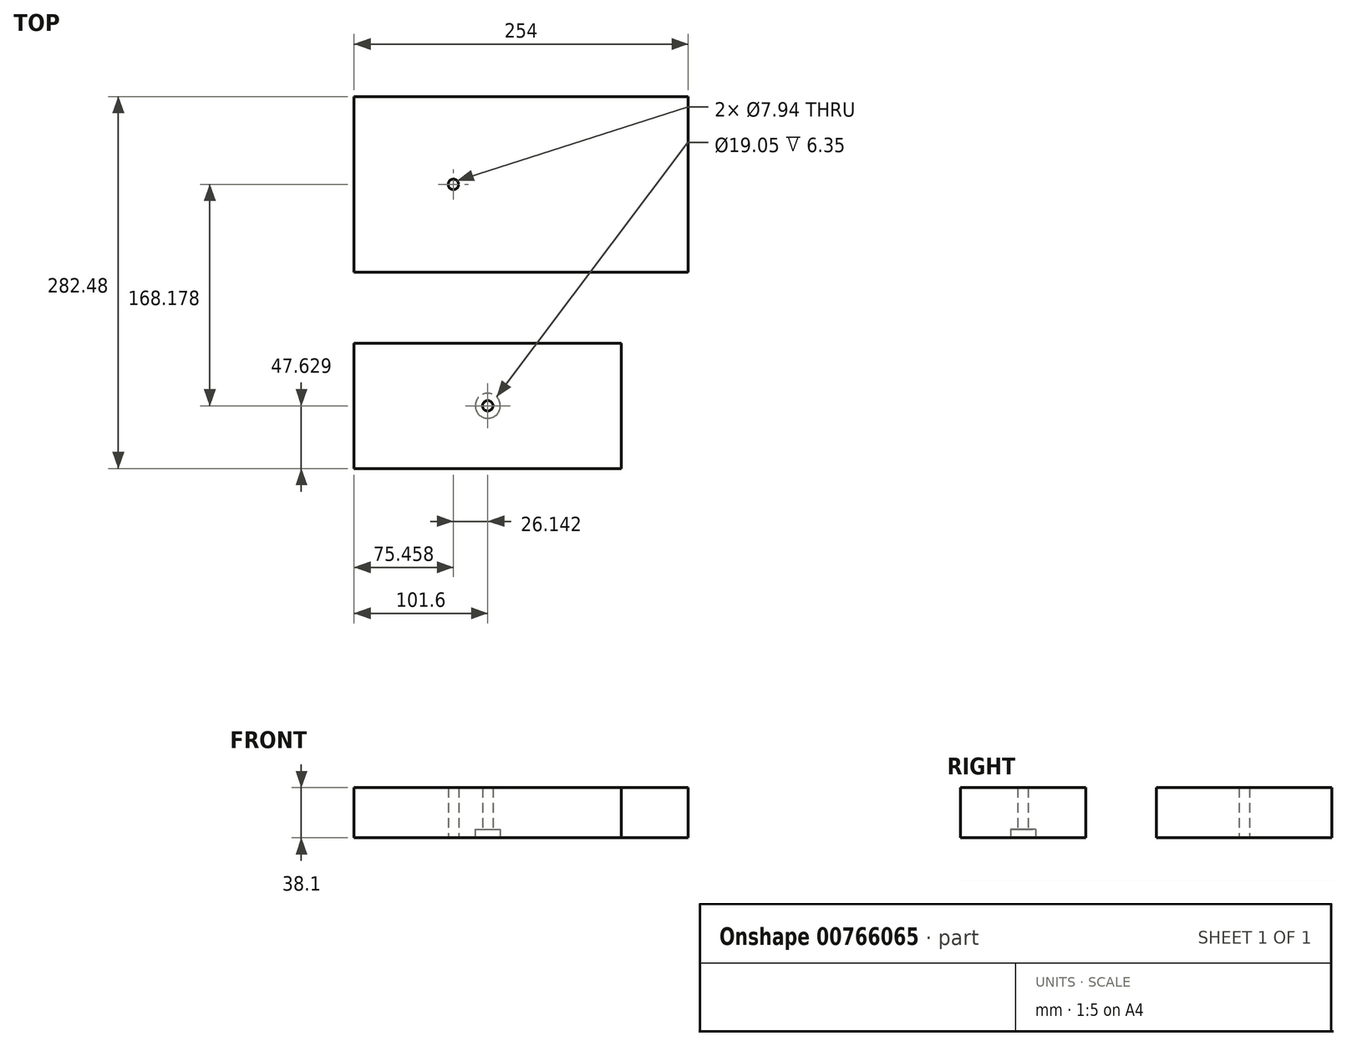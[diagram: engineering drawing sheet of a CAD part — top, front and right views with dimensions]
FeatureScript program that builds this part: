
annotation { "Feature Type Name" : "Feature", "Feature Type Description" : "" }
export const myFeature = defineFeature(function(context is Context, id is Id, definition is map)
    precondition{}
    {
        {
            var Q0;
            Q0=qCreatedBy(makeId("Right.planeOp"),FACE);
            var sketch = newSketch(context, id + "F0", { "sketchPlane" : qUnion([Q0])});
            skLineSegment(sketch, "E0.bottom", {"start": v(-58.9, 18.4) * mm, "end": v(36.34, 18.4) * mm});
            skLineSegment(sketch, "E0.top", {"start": v(-58.9, 56.5) * mm, "end": v(36.34, 56.5) * mm});
            skLineSegment(sketch, "E0.left", {"start": v(-58.9, 18.4) * mm, "end": v(-58.9, 56.5) * mm});
            skLineSegment(sketch, "E0.right", {"start": v(36.34, 18.4) * mm, "end": v(36.34, 56.5) * mm});
            skLineSegment(sketch, "E1.bottom", {"start": v(90.22, 18.4) * mm, "end": v(223.57, 18.4) * mm});
            skLineSegment(sketch, "E1.top", {"start": v(90.22, 56.5) * mm, "end": v(223.57, 56.5) * mm});
            skLineSegment(sketch, "E1.left", {"start": v(90.22, 18.4) * mm, "end": v(90.22, 56.5) * mm});
            skLineSegment(sketch, "E1.right", {"start": v(223.57, 18.4) * mm, "end": v(223.57, 56.5) * mm});
            skSolve(sketch);
        }
        {
            var Q0;
            Q0=makeQuery(id+"F0.imprint","IMPRINT",FACE,{"disambiguationData":[TD([[makeQuery(id+"F0.imprint","IMPRINT",EDGE,{"derivedFrom":sQuery(id+"F0.wireOp",EDGE,"E0.bottom")}),1.0]])]});
            extrude(context, id + "F1", {"entities" : qUnion([Q0]), "depth" : 203.2 * mm, "offsetDistance" : 25.4 * mm});
        }
        {
            var Q0;
            Q0=makeQuery(id+"F0.imprint","IMPRINT",FACE,{"disambiguationData":[TD([[makeQuery(id+"F0.imprint","IMPRINT",EDGE,{"derivedFrom":sQuery(id+"F0.wireOp",EDGE,"E1.bottom")}),1.0]])]});
            extrude(context, id + "F2", {"entities" : qUnion([Q0]), "depth" : 254 * mm, "offsetDistance" : 25.4 * mm});
        }
        {
            var Q0;
            Q0=qCreatedBy(makeId("Top.planeOp"),FACE);
            var sketch = newSketch(context, id + "F3", { "sketchPlane" : qUnion([Q0])});
            skPoint(sketch, "E2.0", {"position": v(0, 156.9) * mm});
            skPoint(sketch, "E3.0", {"position": v(0, -11.28) * mm});
            skPoint(sketch, "E4", {"position": v(75.46, 156.9) * mm});
            skPoint(sketch, "E5.0", {"position": v(101.6, 36.34) * mm});
            skPoint(sketch, "E6", {"position": v(101.6, -11.28) * mm});
            skSolve(sketch);
        }
        {
            var Q0;
            Q0=sQuery(id+"F3.wireOp",VERTEX,"E6");
            var Q1;
            Q1=makeQuery(id+"F1.opExtrude","SWEPT_BODY",BODY,{"disambiguationData":[OSD([sQuery(id+"F0.wireOp",EDGE,"E0.bottom"),sQuery(id+"F0.wireOp",EDGE,"E0.top"),sQuery(id+"F0.wireOp",EDGE,"E0.left"),sQuery(id+"F0.wireOp",EDGE,"E0.right")])]});
            hole(context, id + "F4", {"style" : HoleStyle.C_BORE, "endStyle" : HoleEndStyle.THROUGH, "oppositeDirection" : true, "holeDiameter" : 7.94 * mm, "cBoreDiameter" : 19.05 * mm, "cBoreDepth" : 6.35 * mm, "majorDiameter" : 6.35 * mm, "isTappedThrough" : true, "tappedDepth" : 12.7 * mm, "tapClearance" : 3, "locations" : qUnion([Q0]), "scope" : qUnion([Q1])});
        }
        {
            var Q0;
            Q0=sQuery(id+"F3.wireOp",VERTEX,"E4");
            var Q1;
            Q1=makeQuery(id+"F2.opExtrude","SWEPT_BODY",BODY,{"disambiguationData":[OSD([sQuery(id+"F0.wireOp",EDGE,"E1.bottom"),sQuery(id+"F0.wireOp",EDGE,"E1.top"),sQuery(id+"F0.wireOp",EDGE,"E1.left"),sQuery(id+"F0.wireOp",EDGE,"E1.right")])]});
            hole(context, id + "F5", {"style" : HoleStyle.SIMPLE, "endStyle" : HoleEndStyle.THROUGH, "oppositeDirection" : true, "holeDiameter" : 7.94 * mm, "majorDiameter" : 6.35 * mm, "isTappedThrough" : true, "tappedDepth" : 12.7 * mm, "tapClearance" : 3, "locations" : qUnion([Q0]), "scope" : qUnion([Q1])});
        }
    });
